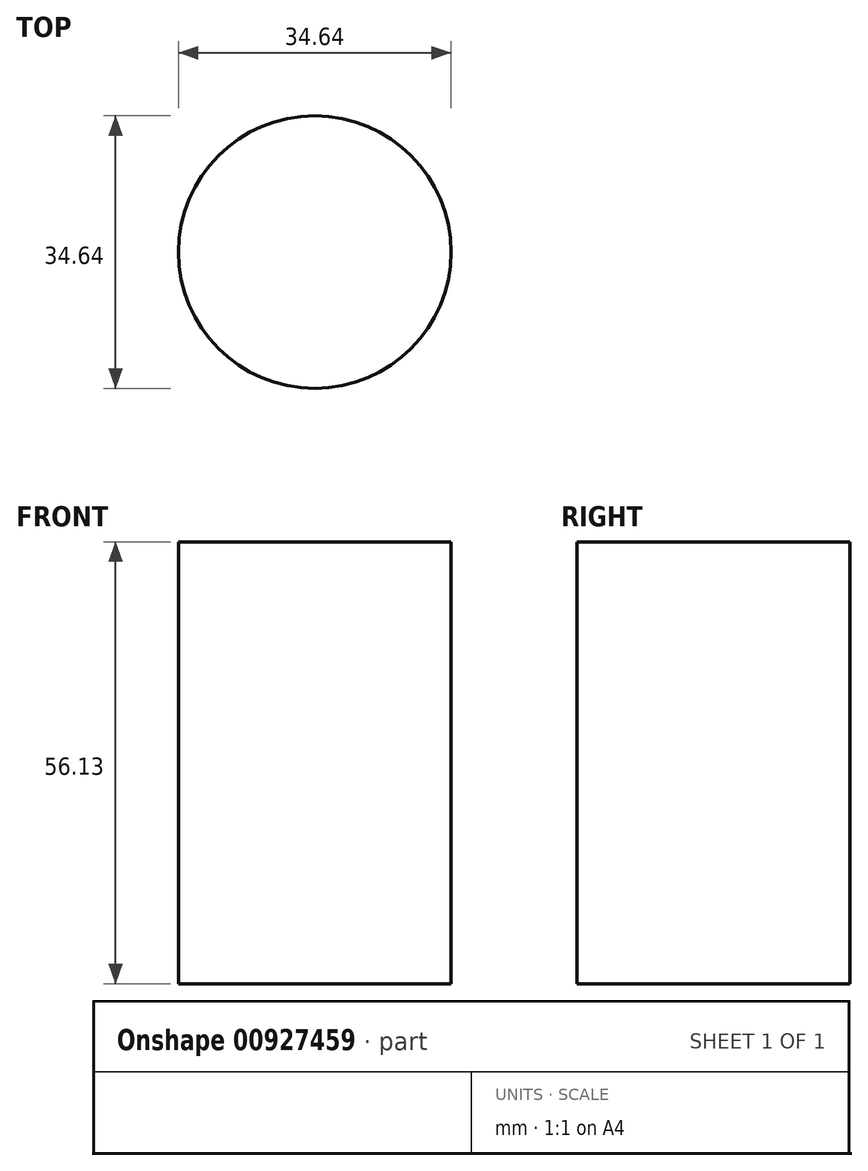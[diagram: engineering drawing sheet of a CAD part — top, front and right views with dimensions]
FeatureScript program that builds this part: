
annotation { "Feature Type Name" : "Feature", "Feature Type Description" : "" }
export const myFeature = defineFeature(function(context is Context, id is Id, definition is map)
    precondition{}
    {
        {
            var Q0;
            Q0=qCreatedBy(makeId("Top.planeOp"),FACE);
            var sketch = newSketch(context, id + "F0", { "sketchPlane" : qUnion([Q0])});
            skCircle(sketch, "E0", {"center": v(0, 0) * mm, "radius": 17.32 * mm});
            skSolve(sketch);
        }
        {
            var Q0;
            Q0 = qSketchRegion(id + "F0", true);
            var Q1;
            Q1=makeQuery(id+"F0.imprint","IMPRINT",FACE,{"disambiguationData":[TD([[makeQuery(id+"F0.imprint","IMPRINT",EDGE,{"derivedFrom":sQuery(id+"F0.wireOp",EDGE,"E0")}),1.0]])]});
            extrude(context, id + "F1", {"entities" : qUnion([Q0, Q1]), "depth" : 56.13 * mm, "offsetDistance" : 25.4 * mm});
        }
    });
